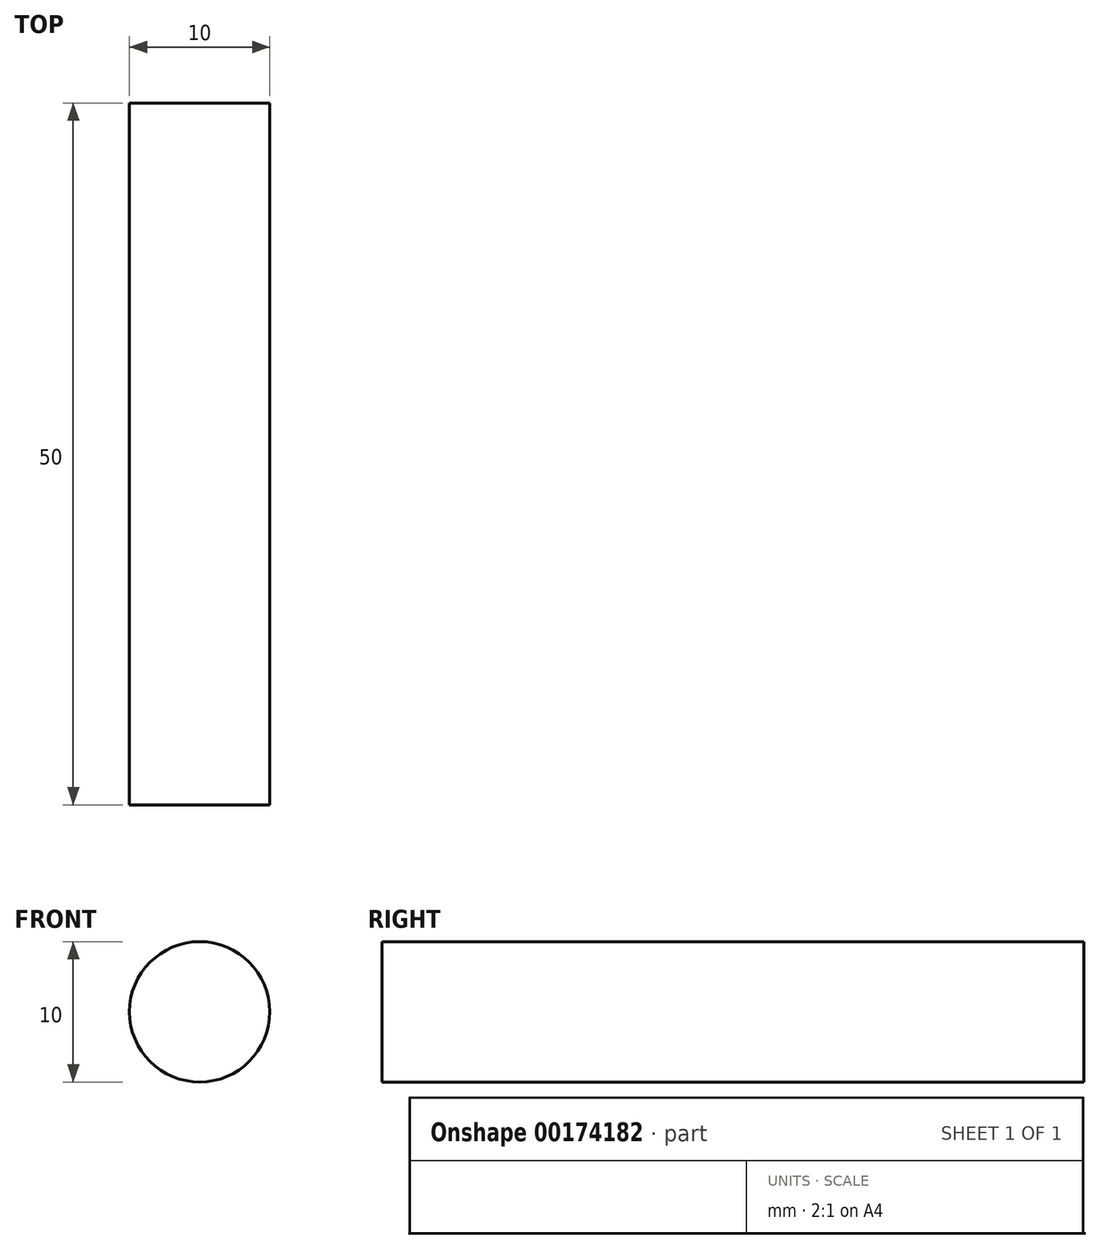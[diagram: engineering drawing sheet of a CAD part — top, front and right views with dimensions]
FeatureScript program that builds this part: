
annotation { "Feature Type Name" : "Feature", "Feature Type Description" : "" }
export const myFeature = defineFeature(function(context is Context, id is Id, definition is map)
    precondition{}
    {
        {
            var Q0;
            Q0=qCreatedBy(makeId("Front.planeOp"),FACE);
            var sketch = newSketch(context, id + "F0", { "sketchPlane" : qUnion([Q0])});
            skCircle(sketch, "E0", {"center": v(0, 0) * mm, "radius": 5 * mm});
            skSolve(sketch);
        }
        {
            var Q0;
            Q0=makeQuery(id+"F0.imprint","IMPRINT",FACE,{"disambiguationData":[TD([[makeQuery(id+"F0.imprint","IMPRINT",EDGE,{"derivedFrom":sQuery(id+"F0.wireOp",EDGE,"E0")}),1.0]])]});
            extrude(context, id + "F1", {"entities" : qUnion([Q0]), "depth" : 25 * mm, "hasSecondDirection" : true, "secondDirectionOppositeDirection" : true, "secondDirectionDepth" : 25 * mm});
        }
    });
